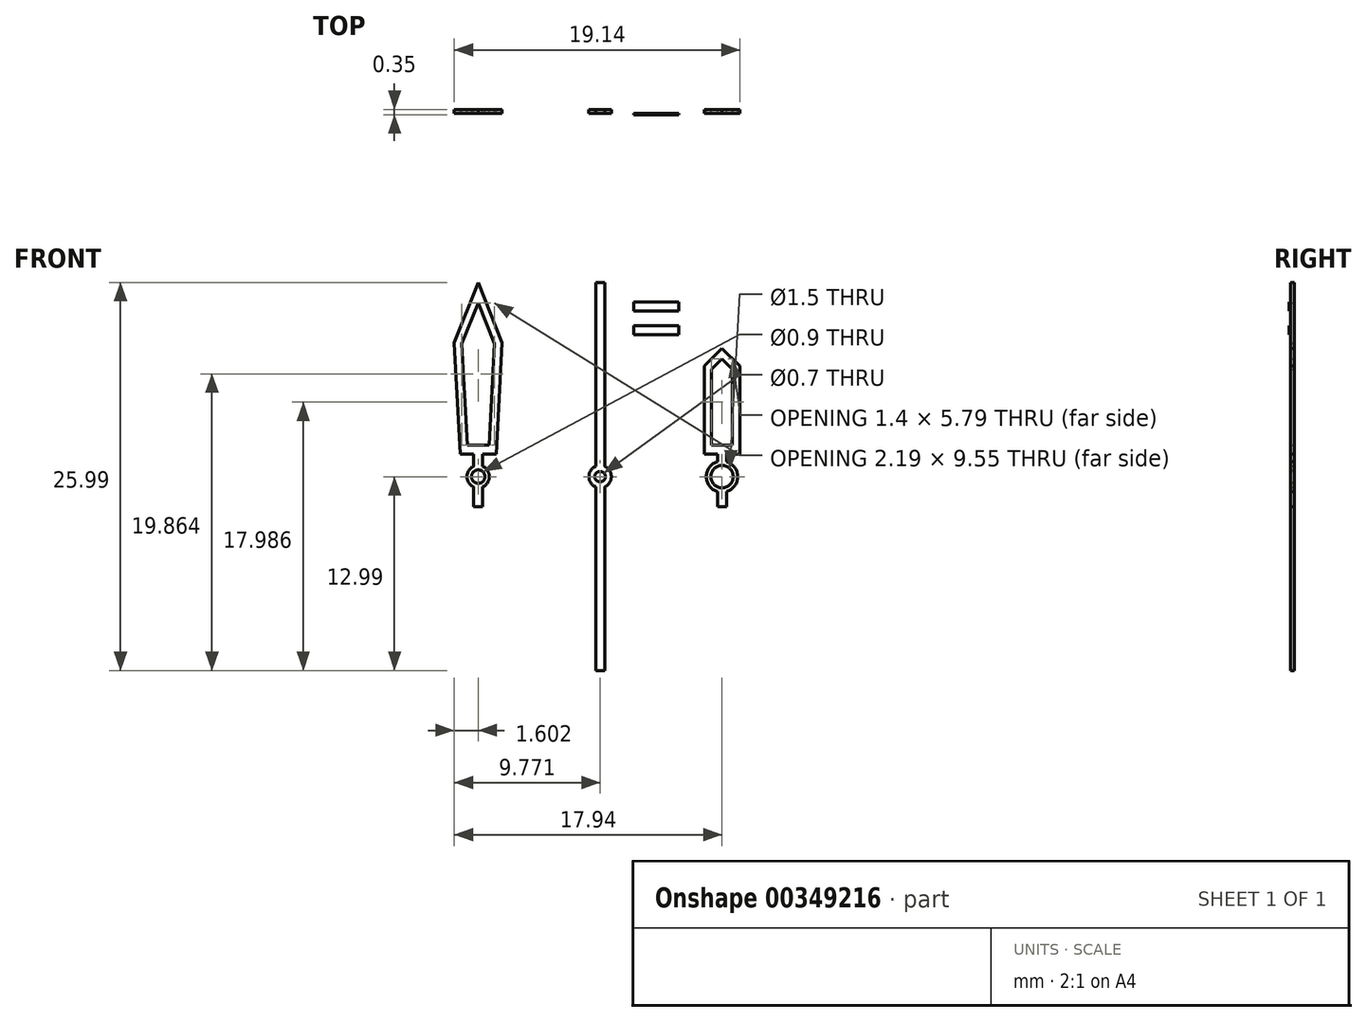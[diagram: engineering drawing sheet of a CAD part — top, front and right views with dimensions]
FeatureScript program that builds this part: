
annotation { "Feature Type Name" : "Feature", "Feature Type Description" : "" }
export const myFeature = defineFeature(function(context is Context, id is Id, definition is map)
    precondition{}
    {
        {
            var Q0;
            Q0=qCreatedBy(makeId("Front.planeOp"),FACE);
            var sketch = newSketch(context, id + "F0", { "sketchPlane" : qUnion([Q0])});
            skLineSegment(sketch, "E0", {"start": v(-36.59, 13) * mm, "end": v(-34.99, 8.98) * mm});
            skCircle(sketch, "E1", {"center": v(-36.59, 0) * mm, "radius": 0.45 * mm});
            skCircle(sketch, "E2.0", {"center": v(-36.59, 0) * mm, "radius": 0.75 * mm});
            skLineSegment(sketch, "E3", {"start": v(-36.29, 0.69) * mm, "end": v(-36.29, 2) * mm});
            skLineSegment(sketch, "E4", {"start": v(-36.29, -0.69) * mm, "end": v(-36.29, -2) * mm});
            skLineSegment(sketch, "E5.MirrorCS", {"start": v(-36.89, 0.69) * mm, "end": v(-36.89, 2) * mm});
            skLineSegment(sketch, "E6.MirrorCS", {"start": v(-36.89, -0.69) * mm, "end": v(-36.89, -2) * mm});
            skLineSegment(sketch, "E7", {"start": v(-36.89, -2) * mm, "end": v(-36.29, -2) * mm});
            skCircle(sketch, "E8", {"center": v(-20.25, 0) * mm, "radius": 0.75 * mm});
            skCircle(sketch, "E9", {"center": v(-20.25, 0) * mm, "radius": 1.05 * mm});
            skLineSegment(sketch, "E10", {"start": v(-19.95, 1) * mm, "end": v(-19.95, 1.5) * mm});
            skLineSegment(sketch, "E11", {"start": v(-20.55, -2) * mm, "end": v(-19.95, -2) * mm});
            skLineSegment(sketch, "E12", {"start": v(-20.55, -1) * mm, "end": v(-20.55, -2) * mm});
            skLineSegment(sketch, "E13", {"start": v(-19.95, -1) * mm, "end": v(-19.95, -2) * mm});
            skCircle(sketch, "E14", {"center": v(-28.42, 0) * mm, "radius": 0.35 * mm});
            skCircle(sketch, "E15", {"center": v(-28.42, 0) * mm, "radius": 0.75 * mm});
            skLineSegment(sketch, "E16", {"start": v(-20.25, 0) * mm, "end": v(-36.59, 0) * mm});
            skLineSegment(sketch, "E17", {"start": v(-36.59, 13) * mm, "end": v(-36.59, 0) * mm});
            skLineSegment(sketch, "E18.MirrorCS", {"start": v(-36.59, 13) * mm, "end": v(-38.19, 8.98) * mm});
            skLineSegment(sketch, "E19", {"start": v(-20.25, 8.6) * mm, "end": v(-20.25, 0) * mm});
            skLineSegment(sketch, "E20.MirrorCS", {"start": v(-20.55, 1) * mm, "end": v(-20.55, 1.5) * mm});
            skLineSegment(sketch, "E21", {"start": v(-36.59, 1.5) * mm, "end": v(-35.39, 1.5) * mm});
            skLineSegment(sketch, "E22", {"start": v(-34.99, 8.98) * mm, "end": v(-35.39, 1.5) * mm});
            skLineSegment(sketch, "E23.MirrorCS", {"start": v(-38.19, 8.98) * mm, "end": v(-37.79, 1.5) * mm});
            skLineSegment(sketch, "E24", {"start": v(-36.59, 1.5) * mm, "end": v(-37.79, 1.5) * mm});
            skLineSegment(sketch, "E25.0", {"start": v(-36.59, 2.1) * mm, "end": v(-35.39, 2.1) * mm});
            skLineSegment(sketch, "E25.1", {"start": v(-36.59, 2.1) * mm, "end": v(-37.79, 2.1) * mm});
            skLineSegment(sketch, "E26", {"start": v(-21.45, 1.5) * mm, "end": v(-19.05, 1.5) * mm});
            skLineSegment(sketch, "E27.0", {"start": v(-21.45, 2.1) * mm, "end": v(-19.05, 2.1) * mm});
            skLineSegment(sketch, "E28", {"start": v(-28.42, 0) * mm, "end": v(-28.42, 13) * mm});
            skLineSegment(sketch, "E29.0", {"start": v(-28.12, 0) * mm, "end": v(-28.12, 13) * mm});
            skLineSegment(sketch, "E30.MirrorCS", {"start": v(-28.72, 0) * mm, "end": v(-28.72, 13) * mm});
            skLineSegment(sketch, "E31", {"start": v(-28.72, 13) * mm, "end": v(-28.12, 13) * mm});
            skLineSegment(sketch, "E32.MirrorCS", {"start": v(-28.12, 0) * mm, "end": v(-28.12, -13) * mm});
            skLineSegment(sketch, "E33.MirrorCS", {"start": v(-28.72, 0) * mm, "end": v(-28.72, -13) * mm});
            skLineSegment(sketch, "E34.MirrorCS", {"start": v(-28.72, -13) * mm, "end": v(-28.12, -13) * mm});
            skLineSegment(sketch, "E35", {"start": v(-28.42, 0) * mm, "end": v(-28.42, -13) * mm});
            skLineSegment(sketch, "E36", {"start": v(-19.05, 1.5) * mm, "end": v(-19.05, 7.4) * mm});
            skLineSegment(sketch, "E37", {"start": v(-19.05, 7.4) * mm, "end": v(-20.25, 8.6) * mm});
            skLineSegment(sketch, "E38", {"start": v(-20.25, 7.9) * mm, "end": v(-19.55, 7.2) * mm});
            skLineSegment(sketch, "E39", {"start": v(-19.55, 7.2) * mm, "end": v(-19.55, 1.5) * mm});
            skLineSegment(sketch, "E40.MirrorCS", {"start": v(-20.25, 7.9) * mm, "end": v(-20.95, 7.2) * mm});
            skLineSegment(sketch, "E41.MirrorCS", {"start": v(-21.45, 7.4) * mm, "end": v(-20.25, 8.6) * mm});
            skLineSegment(sketch, "E42.MirrorCS", {"start": v(-20.95, 7.2) * mm, "end": v(-20.95, 1.5) * mm});
            skLineSegment(sketch, "E43.MirrorCS", {"start": v(-21.45, 1.5) * mm, "end": v(-21.45, 7.4) * mm});
            skLineSegment(sketch, "E44", {"start": v(-36.59, 11.65) * mm, "end": v(-35.5, 8.9) * mm});
            skLineSegment(sketch, "E45", {"start": v(-35.5, 8.9) * mm, "end": v(-35.85, 2.1) * mm});
            skLineSegment(sketch, "E46.MirrorCS", {"start": v(-36.59, 11.65) * mm, "end": v(-37.68, 8.9) * mm});
            skLineSegment(sketch, "E47.MirrorCS", {"start": v(-37.68, 8.9) * mm, "end": v(-37.32, 2.1) * mm});
            skLineSegment(sketch, "E48.bottom", {"start": v(-26.16, 11.7) * mm, "end": v(-23.16, 11.7) * mm});
            skLineSegment(sketch, "E48.top", {"start": v(-26.16, 11.1) * mm, "end": v(-23.16, 11.1) * mm});
            skLineSegment(sketch, "E48.left", {"start": v(-26.16, 11.7) * mm, "end": v(-26.16, 11.1) * mm});
            skLineSegment(sketch, "E48.right", {"start": v(-23.16, 11.7) * mm, "end": v(-23.16, 11.1) * mm});
            skLineSegment(sketch, "E49.bottom", {"start": v(-26.16, 10.1) * mm, "end": v(-23.16, 10.1) * mm});
            skLineSegment(sketch, "E49.top", {"start": v(-26.16, 9.5) * mm, "end": v(-23.16, 9.5) * mm});
            skLineSegment(sketch, "E49.left", {"start": v(-26.16, 10.1) * mm, "end": v(-26.16, 9.5) * mm});
            skLineSegment(sketch, "E49.right", {"start": v(-23.16, 10.1) * mm, "end": v(-23.16, 9.5) * mm});
            skSolve(sketch);
        }
        {
            var Q0;
            Q0=qSketchRegion(id+"F0",true);
            var Q1;
            {var subQ0=sQuery(id+"F0.wireOp",EDGE,"d177a6a1-e401-462f-85d2-7b86f48335750.MirrorCS");var subQ1=sQuery(id+"F0.wireOp",EDGE,"215cdf59-a4c0-4674-9381-4349cfd28c600.MirrorCS");var subQ2=makeQuery(id+"F0.imprint","INTERSECT",VERTEX,{"derivedFrom":[subQ1,subQ0]});Q1=makeQuery(id+"F0.imprint","IMPRINT",FACE,{"disambiguationData":[TD([[makeQuery(id+"F0.imprint","IMPRINT",EDGE,{"disambiguationData":[TD([[subQ2,1.0]])],"derivedFrom":subQ1}),1.0]])]});}
            var Q2;
            {var subQ0=sQuery(id+"F0.wireOp",EDGE,"RracIFim-sfU7-J9re-uFhn-TZIEqMmSXRwO");var subQ1=sQuery(id+"F0.wireOp",EDGE,"TZlwwtPB-qzDZ-59c8-vJeO-k9AsrddVfFom");var subQ2=makeQuery(id+"F0.imprint","INTERSECT",VERTEX,{"derivedFrom":[subQ1,subQ0]});Q2=makeQuery(id+"F0.imprint","IMPRINT",FACE,{"disambiguationData":[TD([[makeQuery(id+"F0.imprint","IMPRINT",EDGE,{"disambiguationData":[TD([[subQ2,-1.0]])],"derivedFrom":subQ1}),1.0]])]});}
            var Q3;
            {var subQ5=sQuery(id+"F0.wireOp",EDGE,"qfoWTzAd-6RBR-ef4f-ruon-Lh11K5Xnfe9l");Q3=makeQuery(id+"F0.imprint","IMPRINT",FACE,{"disambiguationData":[TD([[makeQuery(id+"F0.imprint","IMPRINT",EDGE,{"derivedFrom":subQ5}),-1.0]])]});}
            var Q4;
            {var subQ6=sQuery(id+"F0.wireOp",EDGE,"vC55PCEN-Tw6F-4sRd-shy5-grdwKRQEr6wB");Q4=makeQuery(id+"F0.imprint","IMPRINT",FACE,{"disambiguationData":[TD([[makeQuery(id+"F0.imprint","IMPRINT",EDGE,{"derivedFrom":subQ6}),-1.0]])]});}
            extrude(context, id + "F1", {"entities" : qUnion([Q0, Q1, Q2, Q3, Q4]), "depth" : .25 * mm});
        }
        {
            var Q0;
            Q0=makeQuery(id+"F1.opExtrude","CAP_FACE",FACE,{"disambiguationData":[OSD([sQuery(id+"F0.wireOp",EDGE,"E48.bottom"),sQuery(id+"F0.wireOp",EDGE,"E48.top"),sQuery(id+"F0.wireOp",EDGE,"E48.left"),sQuery(id+"F0.wireOp",EDGE,"E48.right")])],"isStart":false});
            var Q1;
            Q1=makeQuery(id+"F1.opExtrude","CAP_FACE",FACE,{"disambiguationData":[OSD([sQuery(id+"F0.wireOp",EDGE,"E49.bottom"),sQuery(id+"F0.wireOp",EDGE,"E49.top"),sQuery(id+"F0.wireOp",EDGE,"E49.left"),sQuery(id+"F0.wireOp",EDGE,"E49.right")])],"isStart":false});
            extrude(context, id + "F2", {"entities" : qUnion([Q0, Q1]), "depth" : 0.1 * mm});
        }
        {
            var Q0;
            Q0=makeQuery(id+"F1.opExtrude","SWEPT_BODY",BODY,{"disambiguationData":[OSD([sQuery(id+"F0.wireOp",EDGE,"E48.bottom"),sQuery(id+"F0.wireOp",EDGE,"E48.top"),sQuery(id+"F0.wireOp",EDGE,"E48.left"),sQuery(id+"F0.wireOp",EDGE,"E48.right")])]});
            deleteBodies(context, id + "F3", {"entities" : qUnion([Q0])});
        }
        {
            var Q0;
            Q0=makeQuery(id+"F1.opExtrude","SWEPT_BODY",BODY,{"disambiguationData":[OSD([sQuery(id+"F0.wireOp",EDGE,"E49.bottom"),sQuery(id+"F0.wireOp",EDGE,"E49.top"),sQuery(id+"F0.wireOp",EDGE,"E49.left"),sQuery(id+"F0.wireOp",EDGE,"E49.right")])]});
            deleteBodies(context, id + "F4", {"entities" : qUnion([Q0])});
        }
    });
